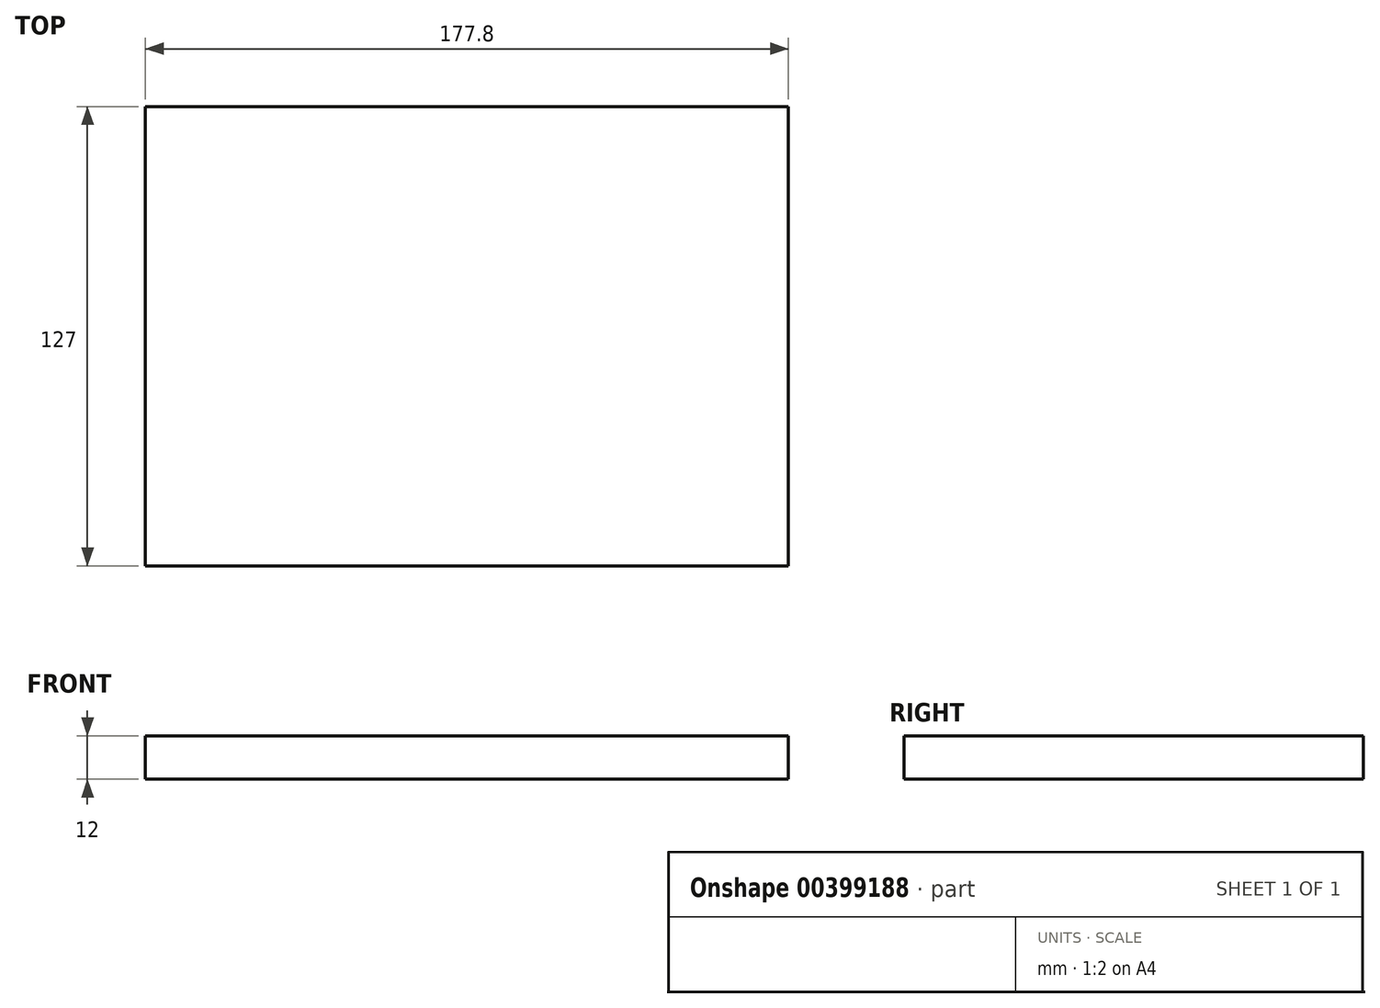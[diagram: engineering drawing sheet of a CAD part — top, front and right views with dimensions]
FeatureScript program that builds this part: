
annotation { "Feature Type Name" : "Feature", "Feature Type Description" : "" }
export const myFeature = defineFeature(function(context is Context, id is Id, definition is map)
    precondition{}
    {
        {
            var Q0;
            Q0=qCreatedBy(makeId("Top.planeOp"),FACE);
            var sketch = newSketch(context, id + "F0", { "sketchPlane" : qUnion([Q0])});
            skLineSegment(sketch, "E0.bottom", {"start": v(0, 0) * mm, "end": v(177.8, 0) * mm});
            skLineSegment(sketch, "E0.top", {"start": v(0, -127) * mm, "end": v(177.8, -127) * mm});
            skLineSegment(sketch, "E0.left", {"start": v(0, 0) * mm, "end": v(0, -127) * mm});
            skLineSegment(sketch, "E0.right", {"start": v(177.8, 0) * mm, "end": v(177.8, -127) * mm});
            skSolve(sketch);
        }
        {
            var Q0;
            Q0 = qSketchRegion(id + "F0", true);
            extrude(context, id + "F1", {"entities" : qUnion([Q0]), "depth" : 12 * mm});
        }
    });
